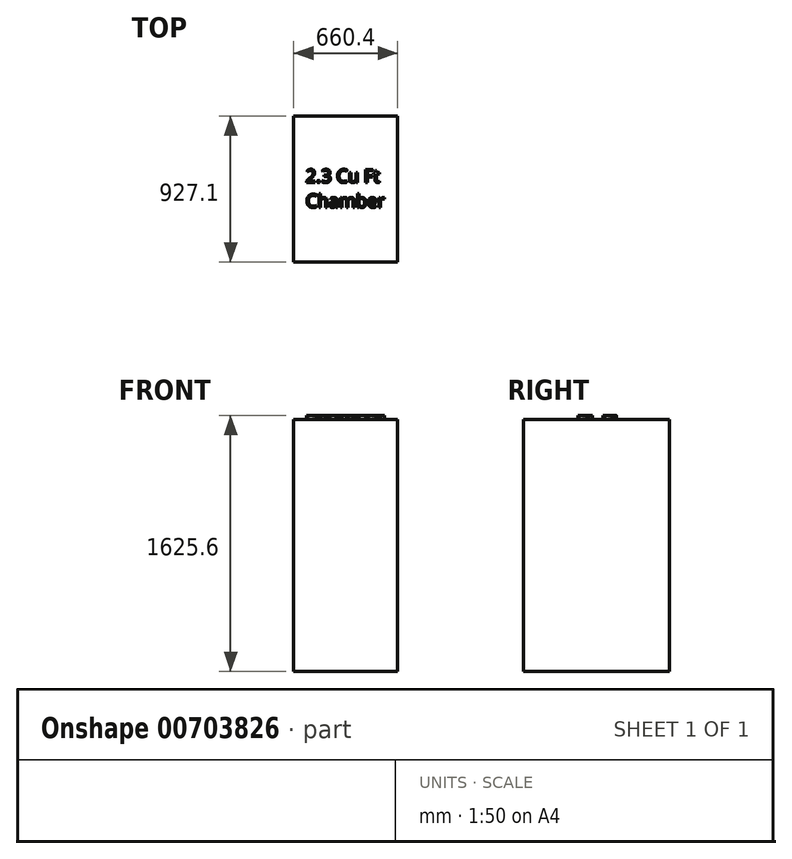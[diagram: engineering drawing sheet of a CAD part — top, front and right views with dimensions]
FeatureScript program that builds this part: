
annotation { "Feature Type Name" : "Feature", "Feature Type Description" : "" }
export const myFeature = defineFeature(function(context is Context, id is Id, definition is map)
    precondition{}
    {
        {
            var Q0;
            Q0=qCreatedBy(makeId("Top.planeOp"),FACE);
            var sketch = newSketch(context, id + "F0", { "sketchPlane" : qUnion([Q0])});
            skLineSegment(sketch, "E0.bottom", {"start": v(330.2, -463.55) * mm, "end": v(-330.2, -463.55) * mm});
            skLineSegment(sketch, "E0.top", {"start": v(330.2, 463.55) * mm, "end": v(-330.2, 463.55) * mm});
            skLineSegment(sketch, "E0.left", {"start": v(330.2, -463.55) * mm, "end": v(330.2, 463.55) * mm});
            skLineSegment(sketch, "E0.right", {"start": v(-330.2, -463.55) * mm, "end": v(-330.2, 463.55) * mm});
            skPoint(sketch, "E0.middle", {"position": v(0, 0) * mm});
            skSolve(sketch);
        }
        {
            var Q0;
            Q0 = qSketchRegion(id + "F0", true);
            extrude(context, id + "F1", {"entities" : qUnion([Q0]), "depth" : 1600.2 * mm, "offsetDistance" : 25.4 * mm});
        }
        {
            var Q0;
            Q0=makeQuery(id+"F1.opExtrude","CAP_FACE",FACE,{"disambiguationData":[OSD([sQuery(id+"F0.wireOp",EDGE,"E0.bottom"),sQuery(id+"F0.wireOp",EDGE,"E0.top"),sQuery(id+"F0.wireOp",EDGE,"E0.left"),sQuery(id+"F0.wireOp",EDGE,"E0.right")])],"isStart":false});
            var sketch = newSketch(context, id + "F2", { "sketchPlane" : qUnion([Q0])});
            skText(sketch, "E1", { "text": "2.3 Cu Ft\nChamber", "fontName": "OpenSans-Regular.ttf"});
            const initialGuessF2  = {"E1": [-0.254, 0.04168, 1, 0, 0.08382]};
            skSetInitialGuess(sketch, initialGuessF2);
            skSolve(sketch);
        }
        {
            var Q0;
            Q0 = qSketchRegion(id + "F2", true);
            extrude(context, id + "F3", {"entities" : qUnion([Q0]), "operationType" : NewBodyOperationType.ADD, "depth" : 25.4 * mm, "offsetDistance" : 25.4 * mm});
        }
    });
